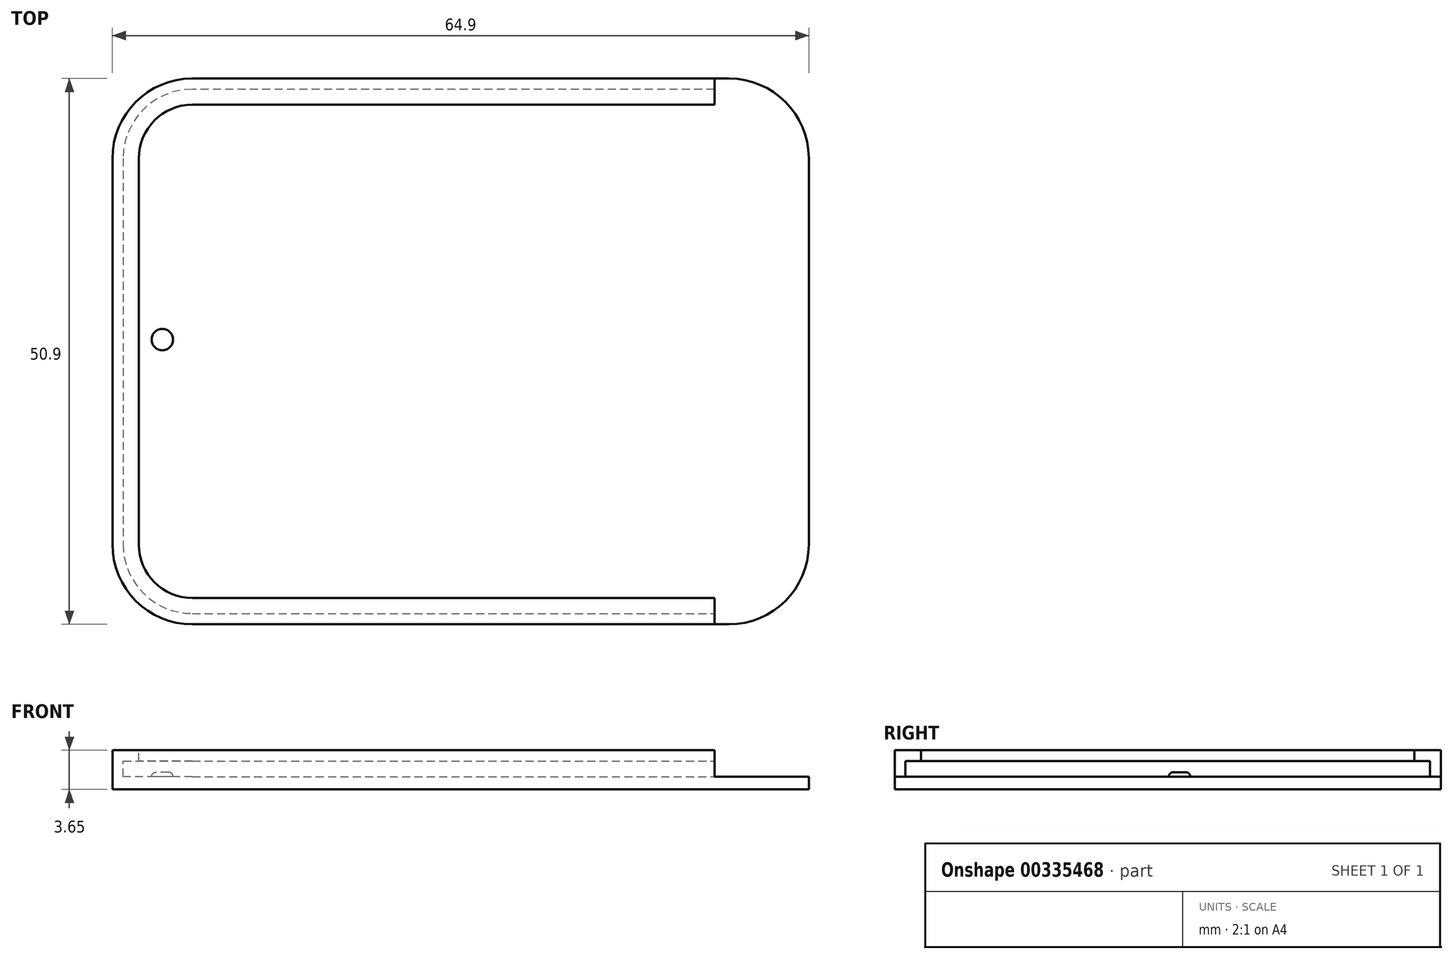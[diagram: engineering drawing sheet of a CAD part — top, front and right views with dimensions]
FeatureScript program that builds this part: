
annotation { "Feature Type Name" : "Feature", "Feature Type Description" : "" }
export const myFeature = defineFeature(function(context is Context, id is Id, definition is map)
    precondition{}
    {
        {
            var Q0;
            Q0=qCreatedBy(makeId("Top.planeOp"),FACE);
            var sketch = newSketch(context, id + "F0", { "sketchPlane" : qUnion([Q0])});
            skLineSegment(sketch, "E0.bottom", {"start": v(-54.58, -22.57) * mm, "end": v(-4.58, -22.57) * mm});
            skLineSegment(sketch, "E0.top", {"start": v(-54.58, 28.33) * mm, "end": v(-4.58, 28.33) * mm});
            skLineSegment(sketch, "E0.left", {"start": v(-62.03, -15.12) * mm, "end": v(-62.03, 20.88) * mm});
            skLineSegment(sketch, "E0.right", {"start": v(2.87, -15.12) * mm, "end": v(2.87, 20.88) * mm});
            skPoint(sketch, "E1.visualSharp", {"position": v(-62.03, 28.33) * mm});
            skArc(sketch, "E1.filletArc", {"start": v(-54.58, 28.33) * mm, "mid": v(-59.84, 26.15) * mm, "end": v(-62.03, 20.88) * mm});
            skPoint(sketch, "E2.visualSharp", {"position": v(2.87, 28.33) * mm});
            skArc(sketch, "E2.filletArc", {"start": v(2.87, 20.88) * mm, "mid": v(0.7, 26.15) * mm, "end": v(-4.58, 28.33) * mm});
            skPoint(sketch, "E3.visualSharp", {"position": v(2.87, -22.57) * mm});
            skArc(sketch, "E3.filletArc", {"start": v(-4.58, -22.57) * mm, "mid": v(0.7, -20.39) * mm, "end": v(2.87, -15.12) * mm});
            skPoint(sketch, "E4.visualSharp", {"position": v(-62.03, -22.57) * mm});
            skArc(sketch, "E4.filletArc", {"start": v(-62.03, -15.12) * mm, "mid": v(-59.84, -20.39) * mm, "end": v(-54.58, -22.57) * mm});
            skSolve(sketch);
        }
        {
            var Q0;
            Q0 = qSketchRegion(id + "F0", true);
            extrude(context, id + "F1", {"entities" : qUnion([Q0]), "depth" : 3.65 * mm});
        }
        {
            var Q0;
            Q0=makeQuery(id+"F1.opExtrude","CAP_FACE",FACE,{"disambiguationData":[OSD([sQuery(id+"F0.wireOp",EDGE,"E0.bottom"),sQuery(id+"F0.wireOp",EDGE,"E0.top"),sQuery(id+"F0.wireOp",EDGE,"E0.left"),sQuery(id+"F0.wireOp",EDGE,"E0.right"),sQuery(id+"F0.wireOp",EDGE,"E1.filletArc"),sQuery(id+"F0.wireOp",EDGE,"E2.filletArc"),sQuery(id+"F0.wireOp",EDGE,"E3.filletArc"),sQuery(id+"F0.wireOp",EDGE,"E4.filletArc")])],"isStart":false});
            var sketch = newSketch(context, id + "F2", { "sketchPlane" : qUnion([Q0])});
            skArc(sketch, "E5.0", {"start": v(1.87, 20.88) * mm, "mid": v(-0.01, 25.44) * mm, "end": v(-4.58, 27.33) * mm});
            skLineSegment(sketch, "E5.1", {"start": v(1.87, -15.12) * mm, "end": v(1.87, 20.88) * mm});
            skLineSegment(sketch, "E5.2", {"start": v(-4.58, 27.33) * mm, "end": v(-54.58, 27.33) * mm});
            skArc(sketch, "E5.3", {"start": v(-4.58, -21.57) * mm, "mid": v(-0.01, -19.68) * mm, "end": v(1.87, -15.12) * mm});
            skArc(sketch, "E5.4", {"start": v(-54.58, 27.33) * mm, "mid": v(-59.14, 25.44) * mm, "end": v(-61.03, 20.88) * mm});
            skLineSegment(sketch, "E5.5", {"start": v(-61.03, 20.88) * mm, "end": v(-61.03, -15.12) * mm});
            skArc(sketch, "E5.6", {"start": v(-61.03, -15.12) * mm, "mid": v(-59.14, -19.68) * mm, "end": v(-54.58, -21.57) * mm});
            skLineSegment(sketch, "E5.7", {"start": v(-54.58, -21.57) * mm, "end": v(-4.58, -21.57) * mm});
            skSolve(sketch);
        }
        {
            var Q0;
            Q0 = qSketchRegion(id + "F2", true);
            extrude(context, id + "F3", {"entities" : qUnion([Q0]), "operationType" : NewBodyOperationType.REMOVE, "oppositeDirection" : true, "depth" : 2.45 * mm});
        }
        {
            var Q0;
            Q0=makeQuery(id+"F1.opExtrude","CAP_FACE",FACE,{"disambiguationData":[OSD([sQuery(id+"F0.wireOp",EDGE,"E0.bottom"),sQuery(id+"F0.wireOp",EDGE,"E0.top"),sQuery(id+"F0.wireOp",EDGE,"E0.left"),sQuery(id+"F0.wireOp",EDGE,"E0.right"),sQuery(id+"F0.wireOp",EDGE,"E1.filletArc"),sQuery(id+"F0.wireOp",EDGE,"E2.filletArc"),sQuery(id+"F0.wireOp",EDGE,"E3.filletArc"),sQuery(id+"F0.wireOp",EDGE,"E4.filletArc")])],"isStart":false});
            var sketch = newSketch(context, id + "F4", { "sketchPlane" : qUnion([Q0])});
            skArc(sketch, "E6.0", {"start": v(0.42, 20.88) * mm, "mid": v(-1.04, 24.42) * mm, "end": v(-4.58, 25.88) * mm});
            skLineSegment(sketch, "E6.1", {"start": v(0.42, -15.12) * mm, "end": v(0.42, 20.88) * mm});
            skLineSegment(sketch, "E6.2", {"start": v(-4.58, 25.88) * mm, "end": v(-54.58, 25.88) * mm});
            skArc(sketch, "E6.3", {"start": v(-4.58, -20.12) * mm, "mid": v(-1.04, -18.65) * mm, "end": v(0.42, -15.12) * mm});
            skArc(sketch, "E6.4", {"start": v(-54.58, 25.88) * mm, "mid": v(-58.11, 24.42) * mm, "end": v(-59.58, 20.88) * mm});
            skLineSegment(sketch, "E6.5", {"start": v(-59.58, 20.88) * mm, "end": v(-59.58, -15.12) * mm});
            skArc(sketch, "E6.6", {"start": v(-59.58, -15.12) * mm, "mid": v(-58.11, -18.65) * mm, "end": v(-54.58, -20.12) * mm});
            skLineSegment(sketch, "E6.7", {"start": v(-54.58, -20.12) * mm, "end": v(-4.58, -20.12) * mm});
            skArc(sketch, "E7.0", {"start": v(1.87, 20.88) * mm, "mid": v(-0.01, 25.44) * mm, "end": v(-4.58, 27.33) * mm});
            skLineSegment(sketch, "E7.1", {"start": v(1.87, -15.12) * mm, "end": v(1.87, 20.88) * mm});
            skLineSegment(sketch, "E7.2", {"start": v(-4.58, 27.33) * mm, "end": v(-54.58, 27.33) * mm});
            skArc(sketch, "E7.3", {"start": v(-4.58, -21.57) * mm, "mid": v(-0.01, -19.68) * mm, "end": v(1.87, -15.12) * mm});
            skArc(sketch, "E7.4", {"start": v(-54.58, 27.33) * mm, "mid": v(-59.14, 25.44) * mm, "end": v(-61.03, 20.88) * mm});
            skLineSegment(sketch, "E7.5", {"start": v(-61.03, 20.88) * mm, "end": v(-61.03, -15.12) * mm});
            skArc(sketch, "E7.6", {"start": v(-61.03, -15.12) * mm, "mid": v(-59.14, -19.68) * mm, "end": v(-54.58, -21.57) * mm});
            skLineSegment(sketch, "E7.7", {"start": v(-54.58, -21.57) * mm, "end": v(-4.58, -21.57) * mm});
            skSolve(sketch);
        }
        {
            var Q0;
            Q0 = qSketchRegion(id + "F4", true);
            extrude(context, id + "F5", {"entities" : qUnion([Q0]), "operationType" : NewBodyOperationType.ADD, "oppositeDirection" : true, "depth" : 1 * mm});
        }
        {
            var Q0;
            Q0=makeQuery(id+"F3.boolean.opBoolean","COPY",FACE,{"derivedFrom":makeQuery(id+"F3.opExtrude","CAP_FACE",FACE,{"disambiguationData":[OSD([sQuery(id+"F2.wireOp",EDGE,"E5.0"),sQuery(id+"F2.wireOp",EDGE,"E5.1"),sQuery(id+"F2.wireOp",EDGE,"E5.2"),sQuery(id+"F2.wireOp",EDGE,"E5.3"),sQuery(id+"F2.wireOp",EDGE,"E5.4"),sQuery(id+"F2.wireOp",EDGE,"E5.5"),sQuery(id+"F2.wireOp",EDGE,"E5.6"),sQuery(id+"F2.wireOp",EDGE,"E5.7")])],"isStart":false})});
            var sketch = newSketch(context, id + "F6", { "sketchPlane" : qUnion([Q0])});
            skLineSegment(sketch, "E8.bottom", {"start": v(-5.9, 32.72) * mm, "end": v(5.63, 32.72) * mm});
            skLineSegment(sketch, "E8.top", {"start": v(-5.9, -28.03) * mm, "end": v(5.63, -28.03) * mm});
            skLineSegment(sketch, "E8.left", {"start": v(-5.9, 32.72) * mm, "end": v(-5.9, -28.03) * mm});
            skLineSegment(sketch, "E8.right", {"start": v(5.63, 32.72) * mm, "end": v(5.63, -28.03) * mm});
            skSolve(sketch);
        }
        {
            var Q0;
            Q0 = qSketchRegion(id + "F6", true);
            extrude(context, id + "F7", {"entities" : qUnion([Q0]), "operationType" : NewBodyOperationType.REMOVE, "depth" : 25 * mm});
        }
        {
            var Q0;
            Q0=makeQuery(id+"F7.boolean.opBoolean","MERGE",FACE,{"derivedFrom":[makeQuery(id+"F3.boolean.opBoolean","COPY",FACE,{"derivedFrom":makeQuery(id+"F3.opExtrude","CAP_FACE",FACE,{"disambiguationData":[OSD([sQuery(id+"F2.wireOp",EDGE,"E5.0"),sQuery(id+"F2.wireOp",EDGE,"E5.1"),sQuery(id+"F2.wireOp",EDGE,"E5.2"),sQuery(id+"F2.wireOp",EDGE,"E5.3"),sQuery(id+"F2.wireOp",EDGE,"E5.4"),sQuery(id+"F2.wireOp",EDGE,"E5.5"),sQuery(id+"F2.wireOp",EDGE,"E5.6"),sQuery(id+"F2.wireOp",EDGE,"E5.7")])],"isStart":false})}),makeQuery(id+"F7.opExtrude","CAP_FACE",FACE,{"disambiguationData":[OSD([sQuery(id+"F6.wireOp",EDGE,"E8.bottom"),sQuery(id+"F6.wireOp",EDGE,"E8.top"),sQuery(id+"F6.wireOp",EDGE,"E8.left"),sQuery(id+"F6.wireOp",EDGE,"E8.right")])],"isStart":true})]});
            var sketch = newSketch(context, id + "F8", { "sketchPlane" : qUnion([Q0])});
            skCircle(sketch, "E9", {"center": v(-57.38, 3.98) * mm, "radius": 1 * mm});
            skSolve(sketch);
        }
        {
            var Q0;
            Q0 = qSketchRegion(id + "F8", true);
            extrude(context, id + "F9", {"entities" : qUnion([Q0]), "operationType" : NewBodyOperationType.ADD, "depth" : .4 * mm});
        }
        {
            var Q0;
            Q0=makeQuery(id+"F9.opExtrude","CAP_EDGE",EDGE,{"disambiguationData":[OSD([sQuery(id+"F8.wireOp",EDGE,"E9")])],"isStart":false});
            fillet(context, id + "F10", {"entities" : qUnion([Q0]), "radius" : .4 * mm, "tangentPropagation" : true, "allowEdgeOverflow" : false});
        }
    });
